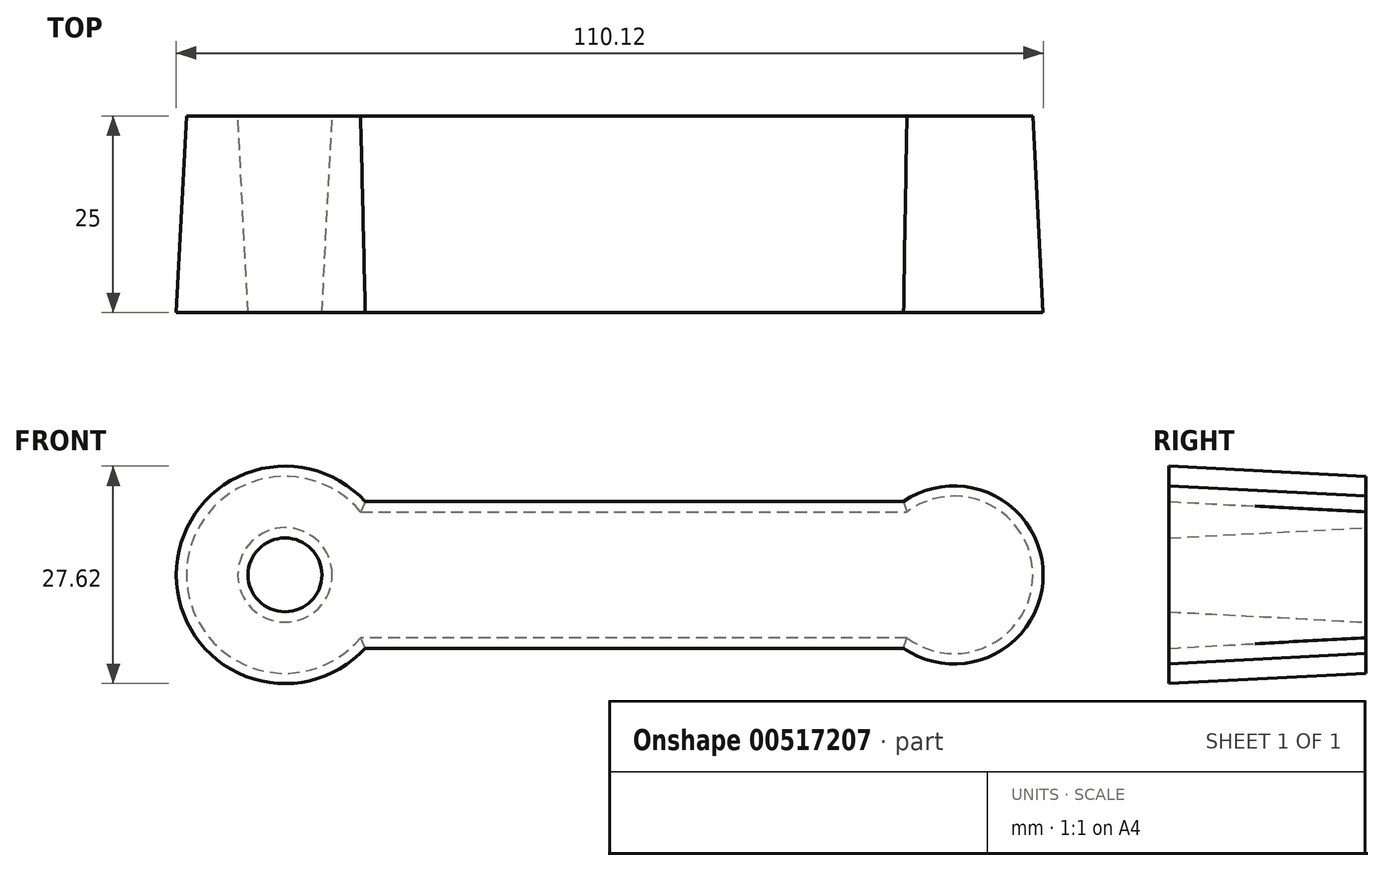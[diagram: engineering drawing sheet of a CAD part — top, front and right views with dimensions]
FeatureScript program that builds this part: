
annotation { "Feature Type Name" : "Feature", "Feature Type Description" : "" }
export const myFeature = defineFeature(function(context is Context, id is Id, definition is map)
    precondition{}
    {
        {
            var Q0;
            Q0=qCreatedBy(makeId("Front.planeOp"),FACE);
            var sketch = newSketch(context, id + "F0", { "sketchPlane" : qUnion([Q0])});
            skCircle(sketch, "E0", {"center": v(-21.38, 0) * mm, "radius": 12.5 * mm});
            skCircle(sketch, "E1", {"center": v(63.62, 0) * mm, "radius": 10 * mm});
            skLineSegment(sketch, "E2", {"start": v(-11.78, 8) * mm, "end": v(57.62, 8) * mm});
            skLineSegment(sketch, "E3.MirrorCS", {"start": v(-11.78, -8) * mm, "end": v(57.62, -8) * mm});
            skCircle(sketch, "E4", {"center": v(-21.38, 0) * mm, "radius": 6 * mm});
            skSolve(sketch);
        }
        {
            var Q0;
            Q0=makeQuery(id+"F0.imprint","IMPRINT",FACE,{"disambiguationData":[TD([[makeQuery(id+"F0.imprint","IMPRINT",EDGE,{"derivedFrom":sQuery(id+"F0.wireOp",EDGE,"E4")}),-1.0]])]});
            var Q1;
            {var subQ0=sQuery(id+"F0.wireOp",EDGE,"E2");Q1=makeQuery(id+"F0.imprint","IMPRINT",FACE,{"disambiguationData":[TD([[makeQuery(id+"F0.imprint","IMPRINT",EDGE,{"derivedFrom":subQ0}),-1.0]])]});}
            var Q2;
            {var subQ0=sQuery(id+"F0.wireOp",EDGE,"E1");var subQ1=makeQuery(id+"F0.imprint","INTERSECT",VERTEX,{"derivedFrom":[subQ0,sQuery(id+"F0.wireOp",EDGE,"E2")]});Q2=makeQuery(id+"F0.imprint","IMPRINT",FACE,{"disambiguationData":[TD([[makeQuery(id+"F0.imprint","IMPRINT",EDGE,{"disambiguationData":[TD([[subQ1,-1.0]])],"derivedFrom":subQ0}),1.0]])]});}
            extrude(context, id + "F1", {"entities" : qUnion([Q0, Q1, Q2]), "depth" : 25 * mm, "offsetDistance" : 25 * mm, "hasDraft" : true, "draftAngle" : 3 * degree});
        }
    });
